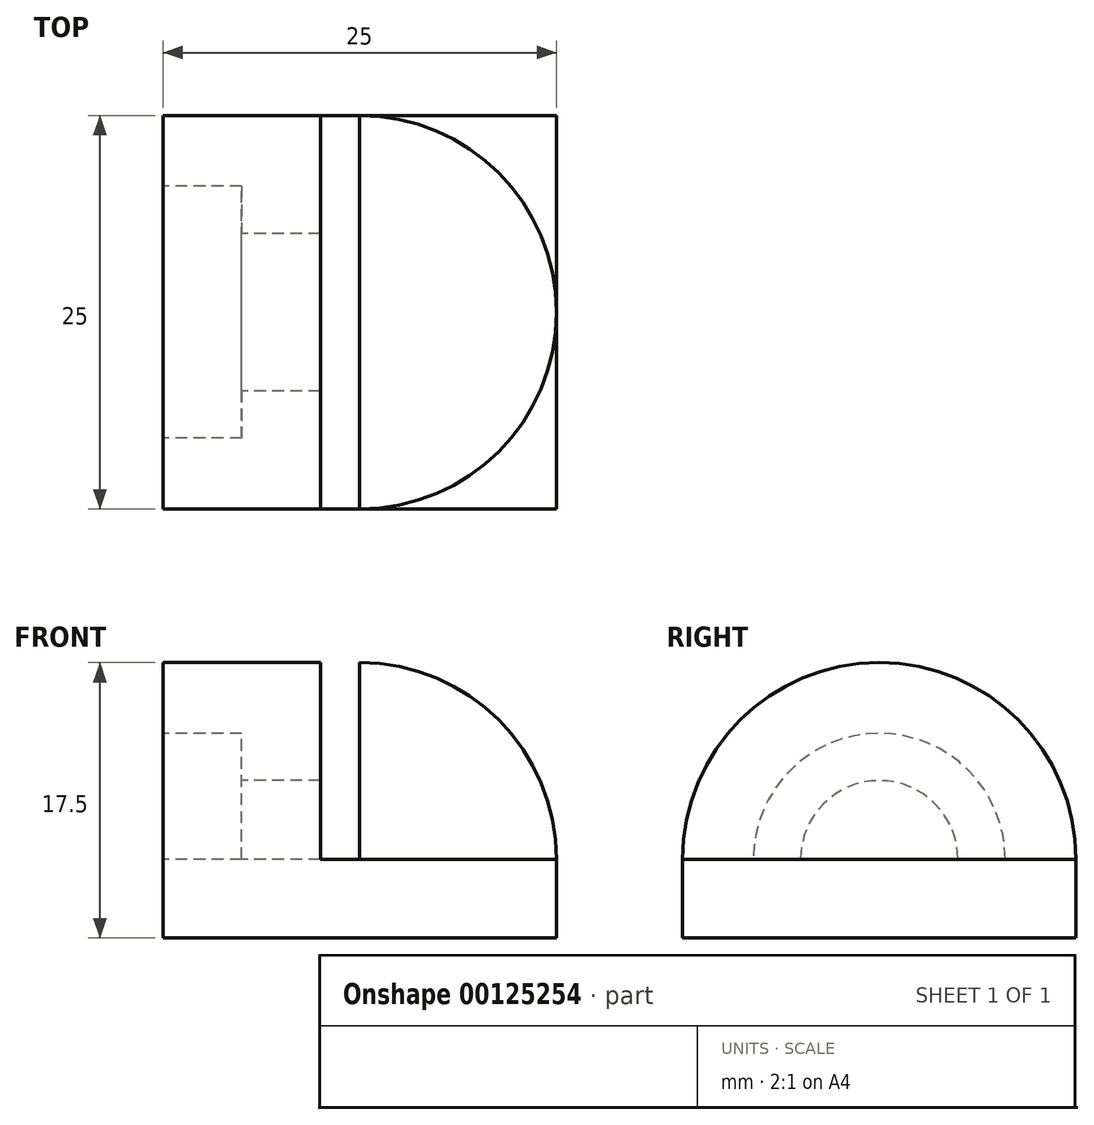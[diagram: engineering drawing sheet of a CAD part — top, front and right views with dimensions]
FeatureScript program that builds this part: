
annotation { "Feature Type Name" : "Feature", "Feature Type Description" : "" }
export const myFeature = defineFeature(function(context is Context, id is Id, definition is map)
    precondition{}
    {
        {
            var Q0;
            Q0=qCreatedBy(makeId("Top.planeOp"),FACE);
            var sketch = newSketch(context, id + "F0", { "sketchPlane" : qUnion([Q0])});
            skLineSegment(sketch, "E0.bottom", {"start": v(12.5, 12.5) * mm, "end": v(-12.5, 12.5) * mm});
            skLineSegment(sketch, "E0.top", {"start": v(12.5, -12.5) * mm, "end": v(-12.5, -12.5) * mm});
            skLineSegment(sketch, "E0.left", {"start": v(12.5, 12.5) * mm, "end": v(12.5, -12.5) * mm});
            skLineSegment(sketch, "E0.right", {"start": v(-12.5, 12.5) * mm, "end": v(-12.5, -12.5) * mm});
            skPoint(sketch, "E0.middle", {"position": v(0, 0) * mm});
            skSolve(sketch);
        }
        {
            var Q0;
            Q0 = qSketchRegion(id + "F0", true);
            extrude(context, id + "F1", {"entities" : qUnion([Q0]), "depth" : 5 * mm});
        }
        {
            var Q0;
            Q0=makeQuery(id+"F1.opExtrude","CAP_FACE",FACE,{"disambiguationData":[OSD([sQuery(id+"F0.wireOp",EDGE,"E0.bottom"),sQuery(id+"F0.wireOp",EDGE,"E0.top"),sQuery(id+"F0.wireOp",EDGE,"E0.left"),sQuery(id+"F0.wireOp",EDGE,"E0.right")])],"isStart":false});
            var sketch = newSketch(context, id + "F2", { "sketchPlane" : qUnion([Q0])});
            skLineSegment(sketch, "E1", {"start": v(0, 12.5) * mm, "end": v(0, -12.5) * mm});
            skArc(sketch, "E2", {"start": v(0, -12.5) * mm, "mid": v(12.5, 0) * mm, "end": v(0, 12.5) * mm});
            skSolve(sketch);
        }
        {
            var Q0;
            {var subQ0=sQuery(id+"F2.wireOp",EDGE,"E1");Q0=makeQuery(id+"F2.imprint","IMPRINT",FACE,{"disambiguationData":[TD([[makeQuery(id+"F2.imprint","IMPRINT",EDGE,{"derivedFrom":subQ0}),1.0]])]});}
            var Q1;
            Q1=sQuery(id+"F2.wireOp",EDGE,"E1");
            revolve(context, id + "F3", {"operationType" : NewBodyOperationType.ADD, "entities" : qUnion([Q0]), "axis" : qUnion([Q1]), "revolveType" : RevolveType.ONE_DIRECTION, "angle" : 90 * degree});
        }
        {
            var Q0;
            Q0=makeQuery(id+"F1.opExtrude","SWEPT_FACE",FACE,{"disambiguationData":[OSD([sQuery(id+"F0.wireOp",EDGE,"E0.right")])]});
            var sketch = newSketch(context, id + "F4", { "sketchPlane" : qUnion([Q0])});
            skArc(sketch, "E3.0.0", {"start": v(12.5, 5) * mm, "mid": v(0, 17.5) * mm, "end": v(-12.5, 5) * mm});
            skLineSegment(sketch, "E3.0.1", {"start": v(-12.5, 5) * mm, "end": v(12.5, 5) * mm});
            skArc(sketch, "E4", {"start": v(8, 5) * mm, "mid": v(0, 13) * mm, "end": v(-8, 5) * mm});
            skArc(sketch, "E5", {"start": v(5, 5) * mm, "mid": v(0, 10) * mm, "end": v(-5, 5) * mm});
            skSolve(sketch);
        }
        {
            var Q0;
            {var subQ0=sQuery(id+"F4.wireOp",EDGE,"E3.0.0");Q0=makeQuery(id+"F4.imprint","IMPRINT",FACE,{"disambiguationData":[TD([[makeQuery(id+"F4.imprint","IMPRINT",EDGE,{"derivedFrom":subQ0}),1.0]])]});}
            var Q1;
            {var subQ0=sQuery(id+"F4.wireOp",EDGE,"E4");Q1=makeQuery(id+"F4.imprint","IMPRINT",FACE,{"disambiguationData":[TD([[makeQuery(id+"F4.imprint","IMPRINT",EDGE,{"derivedFrom":subQ0}),1.0]])]});}
            extrude(context, id + "F5", {"entities" : qUnion([Q0, Q1]), "operationType" : NewBodyOperationType.ADD, "oppositeDirection" : true, "depth" : 10 * mm});
        }
        {
            var Q0;
            {var subQ0=sQuery(id+"F4.wireOp",EDGE,"E4");Q0=makeQuery(id+"F4.imprint","IMPRINT",FACE,{"disambiguationData":[TD([[makeQuery(id+"F4.imprint","IMPRINT",EDGE,{"derivedFrom":subQ0}),1.0]])]});}
            extrude(context, id + "F6", {"entities" : qUnion([Q0]), "operationType" : NewBodyOperationType.REMOVE, "oppositeDirection" : true, "depth" : 5 * mm});
        }
    });
